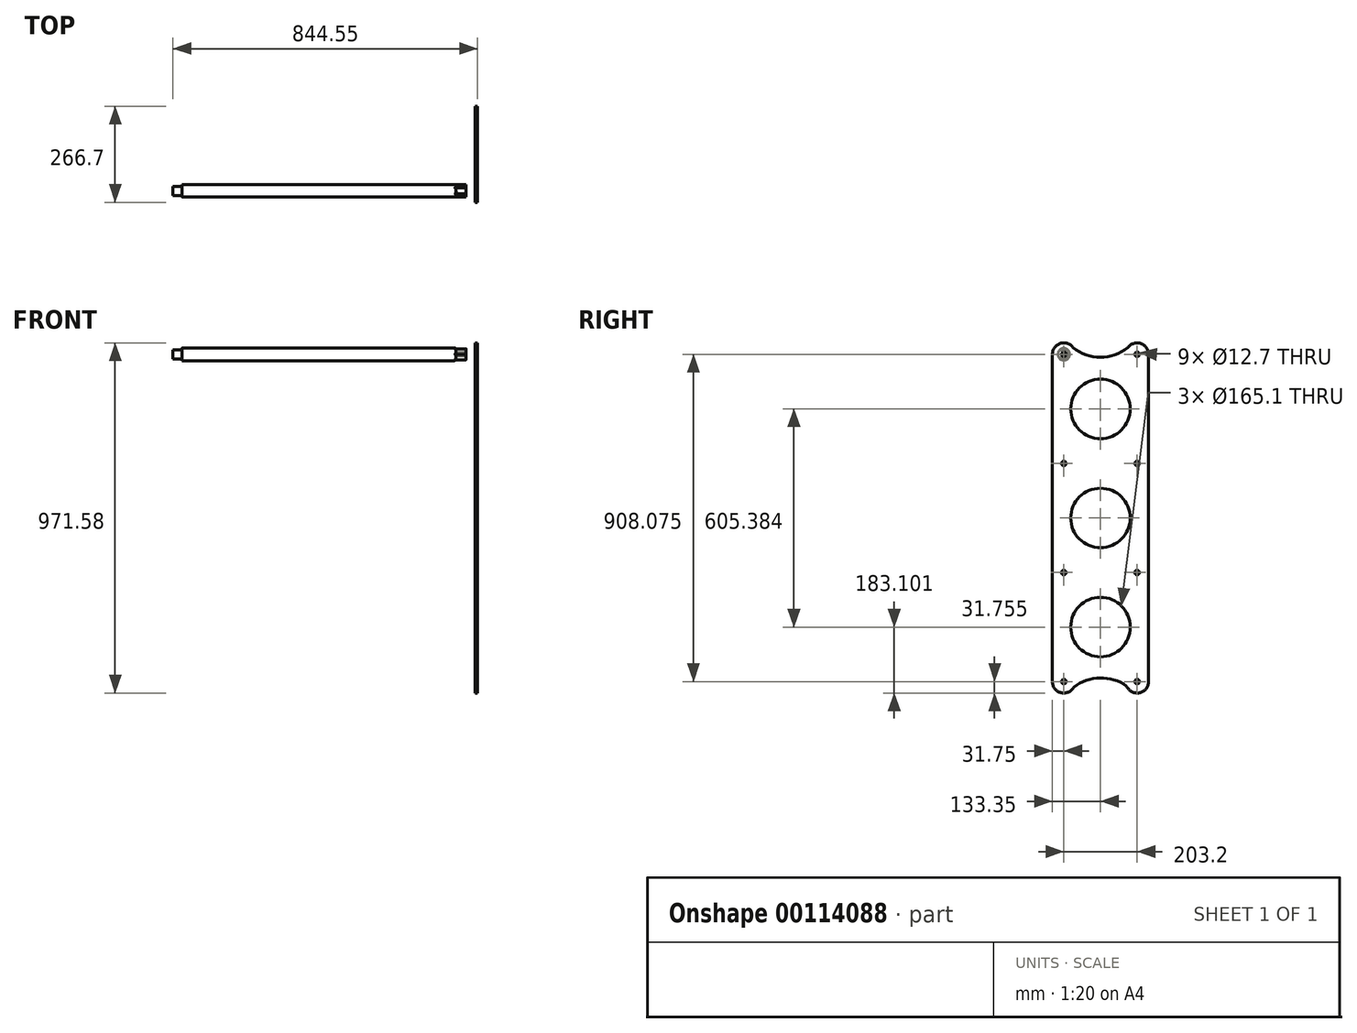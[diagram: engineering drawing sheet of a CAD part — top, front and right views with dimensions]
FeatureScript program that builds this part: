
annotation { "Feature Type Name" : "Feature", "Feature Type Description" : "" }
export const myFeature = defineFeature(function(context is Context, id is Id, definition is map)
    precondition{}
    {
        {
            var Q0;
            Q0=qCreatedBy(makeId("Right.planeOp"),FACE);
            var sketch = newSketch(context, id + "F0", { "sketchPlane" : qUnion([Q0])});
            skCircle(sketch, "E0", {"center": v(0, 0) * mm, "radius": 12.57 * mm});
            skSolve(sketch);
        }
        {
            var Q0;
            Q0 = qSketchRegion(id + "F0", true);
            extrude(context, id + "F1", {"entities" : qUnion([Q0]), "depth" : 25.4 * mm});
        }
        {
            var Q0;
            Q0=makeQuery(id+"F1.opExtrude","CAP_FACE",FACE,{"disambiguationData":[OSD([sQuery(id+"F0.wireOp",EDGE,"E0")])],"isStart":false});
            var sketch = newSketch(context, id + "F2", { "sketchPlane" : qUnion([Q0])});
            skCircle(sketch, "E1", {"center": v(0, 0) * mm, "radius": 17.53 * mm});
            skSolve(sketch);
        }
        {
            var Q0;
            Q0 = qSketchRegion(id + "F2", true);
            extrude(context, id + "F3", {"entities" : qUnion([Q0]), "operationType" : NewBodyOperationType.ADD, "depth" : 787.4 * mm});
        }
        {
            var Q0;
            Q0=makeQuery(id+"F3.opExtrude","CAP_FACE",FACE,{"disambiguationData":[OSD([sQuery(id+"F2.wireOp",EDGE,"E1")])],"isStart":false});
            var sketch = newSketch(context, id + "F4", { "sketchPlane" : qUnion([Q0])});
            skPoint(sketch, "E2", {"position": v(0, 0) * mm});
            skSolve(sketch);
        }
        {
            var Q0;
            Q0=sQuery(id+"F4.wireOp",VERTEX,"E2");
            var Q1;
            Q1=makeQuery(id+"F1.opExtrude","SWEPT_BODY",BODY,{"disambiguationData":[OSD([sQuery(id+"F0.wireOp",EDGE,"E0")])]});
            hole(context, id + "F5", {"style" : HoleStyle.SIMPLE, "endStyle" : HoleEndStyle.BLIND, "holeDiameter" : 12.7 * mm, "holeDepth" : 25.4 * mm, "startFromSketch" : true, "locations" : qUnion([Q0]), "scope" : qUnion([Q1])});
        }
        {
            var Q0;
            Q0=makeQuery(id+"F3.opExtrude","CAP_FACE",FACE,{"disambiguationData":[OSD([sQuery(id+"F2.wireOp",EDGE,"E1")])],"isStart":false});
            var sketch = newSketch(context, id + "F6", { "sketchPlane" : qUnion([Q0])});
            skCircle(sketch, "E3.cCircle", {"center": v(0, 0) * mm, "radius": 15.23 * mm, "construction": true});
            skLineSegment(sketch, "E3.0", {"start": v(-8.8, 15.23) * mm, "end": v(8.8, 15.23) * mm});
            skLineSegment(sketch, "E3.1", {"start": v(8.8, 15.23) * mm, "end": v(17.59, 0) * mm});
            skLineSegment(sketch, "E3.2", {"start": v(17.59, 0) * mm, "end": v(8.8, -15.23) * mm});
            skLineSegment(sketch, "E3.3", {"start": v(8.8, -15.23) * mm, "end": v(-8.8, -15.23) * mm});
            skLineSegment(sketch, "E3.4", {"start": v(-8.8, -15.23) * mm, "end": v(-17.59, 0) * mm});
            skLineSegment(sketch, "E3.5", {"start": v(-17.59, 0) * mm, "end": v(-8.8, 15.23) * mm});
            skPoint(sketch, "E3.0.midPoint", {"position": v(0, 15.23) * mm});
            skCircle(sketch, "E4", {"center": v(0, 0) * mm, "radius": 17.59 * mm});
            skSolve(sketch);
        }
        {
            var Q0;
            Q0=makeQuery(id+"F6.imprint","IMPRINT",FACE,{"disambiguationData":[TD([[makeQuery(id+"F6.imprint","IMPRINT",EDGE,{"derivedFrom":makeQuery(id+"F5.hole-0.boolean.opBoolean","COPY",EDGE,{"derivedFrom":makeQuery(id+"F5.hole-0.opRevolve","SWEPT_EDGE",EDGE,{"disambiguationData":[OSD([sQuery(id+"F5.hole-0.sketch.wireOp",EDGE,"core_line_2"),sQuery(id+"F5.hole-0.sketch.wireOp",EDGE,"core_line_3")])]})})}),1.0]])]});
            var Q1;
            {var subQ0=sQuery(id+"F6.wireOp",EDGE,"E3.0");var subQ1=makeQuery(id+"F3.opExtrude","CAP_EDGE",EDGE,{"disambiguationData":[OSD([sQuery(id+"F2.wireOp",EDGE,"E1")])],"isStart":false});var subQ2=makeQuery(id+"F6.imprint","INTERSECT",VERTEX,{"disambiguationData":[OD(0.0)],"derivedFrom":[subQ1,subQ0]});Q1=makeQuery(id+"F6.imprint","IMPRINT",FACE,{"disambiguationData":[TD([[makeQuery(id+"F6.imprint","IMPRINT",EDGE,{"disambiguationData":[TD([[subQ2,-1.0]])],"derivedFrom":subQ0}),1.0]])]});}
            var Q2;
            {var subQ0=sQuery(id+"F6.wireOp",EDGE,"E3.1");var subQ1=makeQuery(id+"F3.opExtrude","CAP_EDGE",EDGE,{"disambiguationData":[OSD([sQuery(id+"F2.wireOp",EDGE,"E1")])],"isStart":false});var subQ2=makeQuery(id+"F6.imprint","INTERSECT",VERTEX,{"disambiguationData":[OD(0.0)],"derivedFrom":[subQ1,subQ0]});Q2=makeQuery(id+"F6.imprint","IMPRINT",FACE,{"disambiguationData":[TD([[makeQuery(id+"F6.imprint","IMPRINT",EDGE,{"disambiguationData":[TD([[subQ2,-1.0]])],"derivedFrom":subQ0}),1.0]])]});}
            var Q3;
            {var subQ0=sQuery(id+"F6.wireOp",EDGE,"E3.2");var subQ1=makeQuery(id+"F3.opExtrude","CAP_EDGE",EDGE,{"disambiguationData":[OSD([sQuery(id+"F2.wireOp",EDGE,"E1")])],"isStart":false});var subQ2=makeQuery(id+"F6.imprint","INTERSECT",VERTEX,{"disambiguationData":[OD(0.0)],"derivedFrom":[subQ1,subQ0]});Q3=makeQuery(id+"F6.imprint","IMPRINT",FACE,{"disambiguationData":[TD([[makeQuery(id+"F6.imprint","IMPRINT",EDGE,{"disambiguationData":[TD([[subQ2,-1.0]])],"derivedFrom":subQ0}),1.0]])]});}
            var Q4;
            {var subQ0=sQuery(id+"F6.wireOp",EDGE,"E3.3");var subQ1=makeQuery(id+"F3.opExtrude","CAP_EDGE",EDGE,{"disambiguationData":[OSD([sQuery(id+"F2.wireOp",EDGE,"E1")])],"isStart":false});var subQ2=makeQuery(id+"F6.imprint","INTERSECT",VERTEX,{"disambiguationData":[OD(0.0)],"derivedFrom":[subQ1,subQ0]});Q4=makeQuery(id+"F6.imprint","IMPRINT",FACE,{"disambiguationData":[TD([[makeQuery(id+"F6.imprint","IMPRINT",EDGE,{"disambiguationData":[TD([[subQ2,-1.0]])],"derivedFrom":subQ0}),1.0]])]});}
            var Q5;
            {var subQ0=sQuery(id+"F6.wireOp",EDGE,"E3.4");var subQ1=makeQuery(id+"F3.opExtrude","CAP_EDGE",EDGE,{"disambiguationData":[OSD([sQuery(id+"F2.wireOp",EDGE,"E1")])],"isStart":false});var subQ2=makeQuery(id+"F6.imprint","INTERSECT",VERTEX,{"disambiguationData":[OD(0.0)],"derivedFrom":[subQ1,subQ0]});Q5=makeQuery(id+"F6.imprint","IMPRINT",FACE,{"disambiguationData":[TD([[makeQuery(id+"F6.imprint","IMPRINT",EDGE,{"disambiguationData":[TD([[subQ2,-1.0]])],"derivedFrom":subQ0}),1.0]])]});}
            var Q6;
            {var subQ0=sQuery(id+"F6.wireOp",EDGE,"E3.5");var subQ1=makeQuery(id+"F3.opExtrude","CAP_EDGE",EDGE,{"disambiguationData":[OSD([sQuery(id+"F2.wireOp",EDGE,"E1")])],"isStart":false});var subQ2=makeQuery(id+"F6.imprint","INTERSECT",VERTEX,{"disambiguationData":[OD(0.0)],"derivedFrom":[subQ1,subQ0]});Q6=makeQuery(id+"F6.imprint","IMPRINT",FACE,{"disambiguationData":[TD([[makeQuery(id+"F6.imprint","IMPRINT",EDGE,{"disambiguationData":[TD([[subQ2,-1.0]])],"derivedFrom":subQ0}),1.0]])]});}
            var Q7;
            {var subQ1=sQuery(id+"F6.wireOp",EDGE,"E3.0");var subQ3=makeQuery(id+"F3.opExtrude","CAP_EDGE",EDGE,{"disambiguationData":[OSD([sQuery(id+"F2.wireOp",EDGE,"E1")])],"isStart":false});var subQ4=makeQuery(id+"F6.imprint","INTERSECT",VERTEX,{"disambiguationData":[OD(0.0)],"derivedFrom":[subQ3,subQ1]});Q7=makeQuery(id+"F6.imprint","IMPRINT",FACE,{"disambiguationData":[TD([[makeQuery(id+"F6.imprint","IMPRINT",EDGE,{"disambiguationData":[TD([[subQ4,1.0]])],"derivedFrom":subQ3}),-1.0]])]});}
            var Q8;
            {var subQ1=sQuery(id+"F6.wireOp",EDGE,"E3.0");var subQ3=makeQuery(id+"F3.opExtrude","CAP_EDGE",EDGE,{"disambiguationData":[OSD([sQuery(id+"F2.wireOp",EDGE,"E1")])],"isStart":false});var subQ4=makeQuery(id+"F6.imprint","INTERSECT",VERTEX,{"disambiguationData":[OD(0.0)],"derivedFrom":[subQ3,subQ1]});Q8=makeQuery(id+"F6.imprint","IMPRINT",FACE,{"disambiguationData":[TD([[makeQuery(id+"F6.imprint","IMPRINT",EDGE,{"disambiguationData":[TD([[subQ4,-1.0]])],"derivedFrom":subQ3}),-1.0]])]});}
            var Q9;
            {var subQ1=sQuery(id+"F6.wireOp",EDGE,"E3.0");var subQ3=makeQuery(id+"F3.opExtrude","CAP_EDGE",EDGE,{"disambiguationData":[OSD([sQuery(id+"F2.wireOp",EDGE,"E1")])],"isStart":false});var subQ4=makeQuery(id+"F6.imprint","INTERSECT",VERTEX,{"disambiguationData":[OD(1.0)],"derivedFrom":[subQ3,subQ1]});Q9=makeQuery(id+"F6.imprint","IMPRINT",FACE,{"disambiguationData":[TD([[makeQuery(id+"F6.imprint","IMPRINT",EDGE,{"disambiguationData":[TD([[subQ4,1.0]])],"derivedFrom":subQ3}),-1.0]])]});}
            var Q10;
            {var subQ1=sQuery(id+"F6.wireOp",EDGE,"E3.1");var subQ3=makeQuery(id+"F3.opExtrude","CAP_EDGE",EDGE,{"disambiguationData":[OSD([sQuery(id+"F2.wireOp",EDGE,"E1")])],"isStart":false});var subQ4=makeQuery(id+"F6.imprint","INTERSECT",VERTEX,{"disambiguationData":[OD(0.0)],"derivedFrom":[subQ3,subQ1]});Q10=makeQuery(id+"F6.imprint","IMPRINT",FACE,{"disambiguationData":[TD([[makeQuery(id+"F6.imprint","IMPRINT",EDGE,{"disambiguationData":[TD([[subQ4,1.0]])],"derivedFrom":subQ3}),-1.0]])]});}
            var Q11;
            {var subQ1=sQuery(id+"F6.wireOp",EDGE,"E3.1");var subQ3=makeQuery(id+"F3.opExtrude","CAP_EDGE",EDGE,{"disambiguationData":[OSD([sQuery(id+"F2.wireOp",EDGE,"E1")])],"isStart":false});var subQ4=makeQuery(id+"F6.imprint","INTERSECT",VERTEX,{"disambiguationData":[OD(1.0)],"derivedFrom":[subQ3,subQ1]});Q11=makeQuery(id+"F6.imprint","IMPRINT",FACE,{"disambiguationData":[TD([[makeQuery(id+"F6.imprint","IMPRINT",EDGE,{"disambiguationData":[TD([[subQ4,1.0]])],"derivedFrom":subQ3}),-1.0]])]});}
            var Q12;
            {var subQ1=sQuery(id+"F6.wireOp",EDGE,"E3.2");var subQ3=makeQuery(id+"F3.opExtrude","CAP_EDGE",EDGE,{"disambiguationData":[OSD([sQuery(id+"F2.wireOp",EDGE,"E1")])],"isStart":false});var subQ4=makeQuery(id+"F6.imprint","INTERSECT",VERTEX,{"disambiguationData":[OD(0.0)],"derivedFrom":[subQ3,subQ1]});Q12=makeQuery(id+"F6.imprint","IMPRINT",FACE,{"disambiguationData":[TD([[makeQuery(id+"F6.imprint","IMPRINT",EDGE,{"disambiguationData":[TD([[subQ4,1.0]])],"derivedFrom":subQ3}),-1.0]])]});}
            var Q13;
            {var subQ1=sQuery(id+"F6.wireOp",EDGE,"E3.2");var subQ3=makeQuery(id+"F3.opExtrude","CAP_EDGE",EDGE,{"disambiguationData":[OSD([sQuery(id+"F2.wireOp",EDGE,"E1")])],"isStart":false});var subQ4=makeQuery(id+"F6.imprint","INTERSECT",VERTEX,{"disambiguationData":[OD(1.0)],"derivedFrom":[subQ3,subQ1]});Q13=makeQuery(id+"F6.imprint","IMPRINT",FACE,{"disambiguationData":[TD([[makeQuery(id+"F6.imprint","IMPRINT",EDGE,{"disambiguationData":[TD([[subQ4,1.0]])],"derivedFrom":subQ3}),-1.0]])]});}
            var Q14;
            {var subQ1=sQuery(id+"F6.wireOp",EDGE,"E3.3");var subQ3=makeQuery(id+"F3.opExtrude","CAP_EDGE",EDGE,{"disambiguationData":[OSD([sQuery(id+"F2.wireOp",EDGE,"E1")])],"isStart":false});var subQ4=makeQuery(id+"F6.imprint","INTERSECT",VERTEX,{"disambiguationData":[OD(0.0)],"derivedFrom":[subQ3,subQ1]});Q14=makeQuery(id+"F6.imprint","IMPRINT",FACE,{"disambiguationData":[TD([[makeQuery(id+"F6.imprint","IMPRINT",EDGE,{"disambiguationData":[TD([[subQ4,1.0]])],"derivedFrom":subQ3}),-1.0]])]});}
            var Q15;
            {var subQ1=sQuery(id+"F6.wireOp",EDGE,"E3.3");var subQ3=makeQuery(id+"F3.opExtrude","CAP_EDGE",EDGE,{"disambiguationData":[OSD([sQuery(id+"F2.wireOp",EDGE,"E1")])],"isStart":false});var subQ4=makeQuery(id+"F6.imprint","INTERSECT",VERTEX,{"disambiguationData":[OD(1.0)],"derivedFrom":[subQ3,subQ1]});Q15=makeQuery(id+"F6.imprint","IMPRINT",FACE,{"disambiguationData":[TD([[makeQuery(id+"F6.imprint","IMPRINT",EDGE,{"disambiguationData":[TD([[subQ4,1.0]])],"derivedFrom":subQ3}),-1.0]])]});}
            var Q16;
            {var subQ1=sQuery(id+"F6.wireOp",EDGE,"E3.4");var subQ3=makeQuery(id+"F3.opExtrude","CAP_EDGE",EDGE,{"disambiguationData":[OSD([sQuery(id+"F2.wireOp",EDGE,"E1")])],"isStart":false});var subQ4=makeQuery(id+"F6.imprint","INTERSECT",VERTEX,{"disambiguationData":[OD(0.0)],"derivedFrom":[subQ3,subQ1]});Q16=makeQuery(id+"F6.imprint","IMPRINT",FACE,{"disambiguationData":[TD([[makeQuery(id+"F6.imprint","IMPRINT",EDGE,{"disambiguationData":[TD([[subQ4,1.0]])],"derivedFrom":subQ3}),-1.0]])]});}
            var Q17;
            {var subQ1=sQuery(id+"F6.wireOp",EDGE,"E3.4");var subQ3=makeQuery(id+"F3.opExtrude","CAP_EDGE",EDGE,{"disambiguationData":[OSD([sQuery(id+"F2.wireOp",EDGE,"E1")])],"isStart":false});var subQ4=makeQuery(id+"F6.imprint","INTERSECT",VERTEX,{"disambiguationData":[OD(1.0)],"derivedFrom":[subQ3,subQ1]});Q17=makeQuery(id+"F6.imprint","IMPRINT",FACE,{"disambiguationData":[TD([[makeQuery(id+"F6.imprint","IMPRINT",EDGE,{"disambiguationData":[TD([[subQ4,1.0]])],"derivedFrom":subQ3}),-1.0]])]});}
            var Q18;
            {var subQ1=sQuery(id+"F6.wireOp",EDGE,"E3.5");var subQ3=makeQuery(id+"F3.opExtrude","CAP_EDGE",EDGE,{"disambiguationData":[OSD([sQuery(id+"F2.wireOp",EDGE,"E1")])],"isStart":false});var subQ4=makeQuery(id+"F6.imprint","INTERSECT",VERTEX,{"disambiguationData":[OD(0.0)],"derivedFrom":[subQ3,subQ1]});Q18=makeQuery(id+"F6.imprint","IMPRINT",FACE,{"disambiguationData":[TD([[makeQuery(id+"F6.imprint","IMPRINT",EDGE,{"disambiguationData":[TD([[subQ4,1.0]])],"derivedFrom":subQ3}),-1.0]])]});}
            extrude(context, id + "F7", {"entities" : qUnion([Q0, Q1, Q2, Q3, Q4, Q5, Q6, Q7, Q8, Q9, Q10, Q11, Q12, Q13, Q14, Q15, Q16, Q17, Q18]), "operationType" : NewBodyOperationType.REMOVE, "oppositeDirection" : true, "depth" : 25.4 * mm});
        }
        {
            var Q0;
            {var subQ0=sQuery(id+"F2.wireOp",EDGE,"E1");Q0=makeQuery(id+"F7.boolean.opBoolean","INTERSECT",EDGE,{"disambiguationData":[OD(1.0)],"derivedFrom":[makeQuery(id+"F3.opExtrude","SWEPT_FACE",FACE,{"disambiguationData":[OSD([subQ0])]}),makeQuery(id+"F7.opExtrude","CAP_FACE",FACE,{"disambiguationData":[OSD([subQ0,sQuery(id+"F6.wireOp",EDGE,"E3.0"),sQuery(id+"F6.wireOp",EDGE,"E3.1"),sQuery(id+"F6.wireOp",EDGE,"E3.2"),sQuery(id+"F6.wireOp",EDGE,"E3.3"),sQuery(id+"F6.wireOp",EDGE,"E3.4"),sQuery(id+"F6.wireOp",EDGE,"E3.5"),sQuery(id+"F6.wireOp",EDGE,"E4")])],"isStart":false})]});}
            var Q1;
            {var subQ0=sQuery(id+"F2.wireOp",EDGE,"E1");Q1=makeQuery(id+"F7.boolean.opBoolean","INTERSECT",EDGE,{"disambiguationData":[OD(0.0)],"derivedFrom":[makeQuery(id+"F3.opExtrude","SWEPT_FACE",FACE,{"disambiguationData":[OSD([subQ0])]}),makeQuery(id+"F7.opExtrude","CAP_FACE",FACE,{"disambiguationData":[OSD([subQ0,sQuery(id+"F6.wireOp",EDGE,"E3.0"),sQuery(id+"F6.wireOp",EDGE,"E3.1"),sQuery(id+"F6.wireOp",EDGE,"E3.2"),sQuery(id+"F6.wireOp",EDGE,"E3.3"),sQuery(id+"F6.wireOp",EDGE,"E3.4"),sQuery(id+"F6.wireOp",EDGE,"E3.5"),sQuery(id+"F6.wireOp",EDGE,"E4")])],"isStart":false})]});}
            var Q2;
            {var subQ0=sQuery(id+"F2.wireOp",EDGE,"E1");Q2=makeQuery(id+"F7.boolean.opBoolean","INTERSECT",EDGE,{"disambiguationData":[OD(2.0)],"derivedFrom":[makeQuery(id+"F3.opExtrude","SWEPT_FACE",FACE,{"disambiguationData":[OSD([subQ0])]}),makeQuery(id+"F7.opExtrude","CAP_FACE",FACE,{"disambiguationData":[OSD([subQ0,sQuery(id+"F6.wireOp",EDGE,"E3.0"),sQuery(id+"F6.wireOp",EDGE,"E3.1"),sQuery(id+"F6.wireOp",EDGE,"E3.2"),sQuery(id+"F6.wireOp",EDGE,"E3.3"),sQuery(id+"F6.wireOp",EDGE,"E3.4"),sQuery(id+"F6.wireOp",EDGE,"E3.5"),sQuery(id+"F6.wireOp",EDGE,"E4")])],"isStart":false})]});}
            var Q3;
            {var subQ0=sQuery(id+"F2.wireOp",EDGE,"E1");Q3=makeQuery(id+"F7.boolean.opBoolean","INTERSECT",EDGE,{"disambiguationData":[OD(3.0)],"derivedFrom":[makeQuery(id+"F3.opExtrude","SWEPT_FACE",FACE,{"disambiguationData":[OSD([subQ0])]}),makeQuery(id+"F7.opExtrude","CAP_FACE",FACE,{"disambiguationData":[OSD([subQ0,sQuery(id+"F6.wireOp",EDGE,"E3.0"),sQuery(id+"F6.wireOp",EDGE,"E3.1"),sQuery(id+"F6.wireOp",EDGE,"E3.2"),sQuery(id+"F6.wireOp",EDGE,"E3.3"),sQuery(id+"F6.wireOp",EDGE,"E3.4"),sQuery(id+"F6.wireOp",EDGE,"E3.5"),sQuery(id+"F6.wireOp",EDGE,"E4")])],"isStart":false})]});}
            var Q4;
            {var subQ0=sQuery(id+"F2.wireOp",EDGE,"E1");Q4=makeQuery(id+"F7.boolean.opBoolean","INTERSECT",EDGE,{"disambiguationData":[OD(4.0)],"derivedFrom":[makeQuery(id+"F3.opExtrude","SWEPT_FACE",FACE,{"disambiguationData":[OSD([subQ0])]}),makeQuery(id+"F7.opExtrude","CAP_FACE",FACE,{"disambiguationData":[OSD([subQ0,sQuery(id+"F6.wireOp",EDGE,"E3.0"),sQuery(id+"F6.wireOp",EDGE,"E3.1"),sQuery(id+"F6.wireOp",EDGE,"E3.2"),sQuery(id+"F6.wireOp",EDGE,"E3.3"),sQuery(id+"F6.wireOp",EDGE,"E3.4"),sQuery(id+"F6.wireOp",EDGE,"E3.5"),sQuery(id+"F6.wireOp",EDGE,"E4")])],"isStart":false})]});}
            var Q5;
            {var subQ0=sQuery(id+"F2.wireOp",EDGE,"E1");Q5=makeQuery(id+"F7.boolean.opBoolean","INTERSECT",EDGE,{"disambiguationData":[OD(5.0)],"derivedFrom":[makeQuery(id+"F3.opExtrude","SWEPT_FACE",FACE,{"disambiguationData":[OSD([subQ0])]}),makeQuery(id+"F7.opExtrude","CAP_FACE",FACE,{"disambiguationData":[OSD([subQ0,sQuery(id+"F6.wireOp",EDGE,"E3.0"),sQuery(id+"F6.wireOp",EDGE,"E3.1"),sQuery(id+"F6.wireOp",EDGE,"E3.2"),sQuery(id+"F6.wireOp",EDGE,"E3.3"),sQuery(id+"F6.wireOp",EDGE,"E3.4"),sQuery(id+"F6.wireOp",EDGE,"E3.5"),sQuery(id+"F6.wireOp",EDGE,"E4")])],"isStart":false})]});}
            chamfer(context, id + "F8", {"entities" : qUnion([Q0, Q1, Q2, Q3, Q4, Q5]), "width" : 5.08 * mm, "tangentPropagation" : true});
        }
        {
            var Q0;
            {var subQ0=sQuery(id+"F2.wireOp",EDGE,"E1");var subQ1=makeQuery(id+"F3.opExtrude","SWEPT_FACE",FACE,{"disambiguationData":[OSD([subQ0])]});Q0=makeQuery(id+"F8.opChamfer","BLEND_EDGE",EDGE,{"blendedFrom":[makeQuery(id+"F7.boolean.opBoolean","INTERSECT",EDGE,{"disambiguationData":[OD(5.0)],"derivedFrom":[subQ1,makeQuery(id+"F7.opExtrude","CAP_FACE",FACE,{"disambiguationData":[OSD([subQ0,sQuery(id+"F6.wireOp",EDGE,"E3.0"),sQuery(id+"F6.wireOp",EDGE,"E3.1"),sQuery(id+"F6.wireOp",EDGE,"E3.2"),sQuery(id+"F6.wireOp",EDGE,"E3.3"),sQuery(id+"F6.wireOp",EDGE,"E3.4"),sQuery(id+"F6.wireOp",EDGE,"E3.5"),sQuery(id+"F6.wireOp",EDGE,"E4")])],"isStart":false})]}),subQ1],"blendedInto":[subQ1]});}
            var Q1;
            {var subQ0=sQuery(id+"F2.wireOp",EDGE,"E1");var subQ1=makeQuery(id+"F3.opExtrude","SWEPT_FACE",FACE,{"disambiguationData":[OSD([subQ0])]});Q1=makeQuery(id+"F8.opChamfer","BLEND_EDGE",EDGE,{"blendedFrom":[makeQuery(id+"F7.boolean.opBoolean","INTERSECT",EDGE,{"disambiguationData":[OD(4.0)],"derivedFrom":[subQ1,makeQuery(id+"F7.opExtrude","CAP_FACE",FACE,{"disambiguationData":[OSD([subQ0,sQuery(id+"F6.wireOp",EDGE,"E3.0"),sQuery(id+"F6.wireOp",EDGE,"E3.1"),sQuery(id+"F6.wireOp",EDGE,"E3.2"),sQuery(id+"F6.wireOp",EDGE,"E3.3"),sQuery(id+"F6.wireOp",EDGE,"E3.4"),sQuery(id+"F6.wireOp",EDGE,"E3.5"),sQuery(id+"F6.wireOp",EDGE,"E4")])],"isStart":false})]}),subQ1],"blendedInto":[subQ1]});}
            var Q2;
            {var subQ0=sQuery(id+"F2.wireOp",EDGE,"E1");var subQ1=makeQuery(id+"F3.opExtrude","SWEPT_FACE",FACE,{"disambiguationData":[OSD([subQ0])]});Q2=makeQuery(id+"F8.opChamfer","BLEND_EDGE",EDGE,{"blendedFrom":[makeQuery(id+"F7.boolean.opBoolean","INTERSECT",EDGE,{"disambiguationData":[OD(0.0)],"derivedFrom":[subQ1,makeQuery(id+"F7.opExtrude","CAP_FACE",FACE,{"disambiguationData":[OSD([subQ0,sQuery(id+"F6.wireOp",EDGE,"E3.0"),sQuery(id+"F6.wireOp",EDGE,"E3.1"),sQuery(id+"F6.wireOp",EDGE,"E3.2"),sQuery(id+"F6.wireOp",EDGE,"E3.3"),sQuery(id+"F6.wireOp",EDGE,"E3.4"),sQuery(id+"F6.wireOp",EDGE,"E3.5"),sQuery(id+"F6.wireOp",EDGE,"E4")])],"isStart":false})]}),subQ1],"blendedInto":[subQ1]});}
            var Q3;
            {var subQ0=sQuery(id+"F2.wireOp",EDGE,"E1");var subQ1=makeQuery(id+"F3.opExtrude","SWEPT_FACE",FACE,{"disambiguationData":[OSD([subQ0])]});Q3=makeQuery(id+"F8.opChamfer","BLEND_EDGE",EDGE,{"blendedFrom":[makeQuery(id+"F7.boolean.opBoolean","INTERSECT",EDGE,{"disambiguationData":[OD(3.0)],"derivedFrom":[subQ1,makeQuery(id+"F7.opExtrude","CAP_FACE",FACE,{"disambiguationData":[OSD([subQ0,sQuery(id+"F6.wireOp",EDGE,"E3.0"),sQuery(id+"F6.wireOp",EDGE,"E3.1"),sQuery(id+"F6.wireOp",EDGE,"E3.2"),sQuery(id+"F6.wireOp",EDGE,"E3.3"),sQuery(id+"F6.wireOp",EDGE,"E3.4"),sQuery(id+"F6.wireOp",EDGE,"E3.5"),sQuery(id+"F6.wireOp",EDGE,"E4")])],"isStart":false})]}),subQ1],"blendedInto":[subQ1]});}
            var Q4;
            {var subQ0=sQuery(id+"F2.wireOp",EDGE,"E1");var subQ1=makeQuery(id+"F3.opExtrude","SWEPT_FACE",FACE,{"disambiguationData":[OSD([subQ0])]});Q4=makeQuery(id+"F8.opChamfer","BLEND_EDGE",EDGE,{"blendedFrom":[makeQuery(id+"F7.boolean.opBoolean","INTERSECT",EDGE,{"disambiguationData":[OD(2.0)],"derivedFrom":[subQ1,makeQuery(id+"F7.opExtrude","CAP_FACE",FACE,{"disambiguationData":[OSD([subQ0,sQuery(id+"F6.wireOp",EDGE,"E3.0"),sQuery(id+"F6.wireOp",EDGE,"E3.1"),sQuery(id+"F6.wireOp",EDGE,"E3.2"),sQuery(id+"F6.wireOp",EDGE,"E3.3"),sQuery(id+"F6.wireOp",EDGE,"E3.4"),sQuery(id+"F6.wireOp",EDGE,"E3.5"),sQuery(id+"F6.wireOp",EDGE,"E4")])],"isStart":false})]}),subQ1],"blendedInto":[subQ1]});}
            var Q5;
            {var subQ0=sQuery(id+"F2.wireOp",EDGE,"E1");var subQ1=makeQuery(id+"F3.opExtrude","SWEPT_FACE",FACE,{"disambiguationData":[OSD([subQ0])]});Q5=makeQuery(id+"F8.opChamfer","BLEND_EDGE",EDGE,{"blendedFrom":[makeQuery(id+"F7.boolean.opBoolean","INTERSECT",EDGE,{"disambiguationData":[OD(1.0)],"derivedFrom":[subQ1,makeQuery(id+"F7.opExtrude","CAP_FACE",FACE,{"disambiguationData":[OSD([subQ0,sQuery(id+"F6.wireOp",EDGE,"E3.0"),sQuery(id+"F6.wireOp",EDGE,"E3.1"),sQuery(id+"F6.wireOp",EDGE,"E3.2"),sQuery(id+"F6.wireOp",EDGE,"E3.3"),sQuery(id+"F6.wireOp",EDGE,"E3.4"),sQuery(id+"F6.wireOp",EDGE,"E3.5"),sQuery(id+"F6.wireOp",EDGE,"E4")])],"isStart":false})]}),subQ1],"blendedInto":[subQ1]});}
            fillet(context, id + "F9", {"entities" : qUnion([Q0, Q1, Q2, Q3, Q4, Q5]), "radius" : 5.08 * mm, "tangentPropagation" : true, "allowEdgeOverflow" : false});
        }
        {
            var Q0;
            Q0=makeQuery(id+"F3.opExtrude","CAP_FACE",FACE,{"disambiguationData":[OSD([sQuery(id+"F2.wireOp",EDGE,"E1")])],"isStart":false});
            cPlane(context, id + "F10", {"entities" : qUnion([Q0]), "cplaneType" : CPlaneType.OFFSET, "offset" : 25.4 * mm, "width" : 152.4 * mm, "height" : 152.4 * mm});
        }
        {
            var Q0;
            Q0=qCreatedBy(id+"F10.planeOp",FACE);
            var sketch = newSketch(context, id + "F11", { "sketchPlane" : qUnion([Q0])});
            skCircle(sketch, "E5", {"center": v(0, 0) * mm, "radius": 6.35 * mm});
            skLineSegment(sketch, "E6", {"start": v(0, 0) * mm, "end": v(6.35, 0) * mm, "construction": true});
            skCircle(sketch, "E7", {"center": v(203.2, 0) * mm, "radius": 6.35 * mm});
            skLineSegment(sketch, "E8", {"start": v(0, 0) * mm, "end": v(0, -6.35) * mm, "construction": true});
            skLineSegment(sketch, "E9", {"start": v(0, -302.7) * mm, "end": v(0, -309.04) * mm, "construction": true});
            skLineSegment(sketch, "E10", {"start": v(0, -605.38) * mm, "end": v(0, -611.73) * mm, "construction": true});
            skCircle(sketch, "E11", {"center": v(0, -302.7) * mm, "radius": 6.35 * mm});
            skCircle(sketch, "E12", {"center": v(0, -605.38) * mm, "radius": 6.35 * mm});
            skCircle(sketch, "E13", {"center": v(0, -908.08) * mm, "radius": 6.35 * mm});
            skCircle(sketch, "E14", {"center": v(203.2, -302.7) * mm, "radius": 6.35 * mm});
            skCircle(sketch, "E15", {"center": v(203.2, -605.38) * mm, "radius": 6.35 * mm});
            skCircle(sketch, "E16", {"center": v(203.2, -908.08) * mm, "radius": 6.35 * mm});
            skArc(sketch, "E17", {"start": v(25.4, 19.04) * mm, "mid": v(-10.04, 30.12) * mm, "end": v(-31.75, 0) * mm});
            skArc(sketch, "E18", {"start": v(234.95, 0) * mm, "mid": v(213.08, 30.17) * mm, "end": v(177.6, 18.78) * mm});
            skArc(sketch, "E19", {"start": v(174.02, -920.6) * mm, "mid": v(209.6, -939.18) * mm, "end": v(234.95, -908.08) * mm});
            skArc(sketch, "E20", {"start": v(-31.75, -908.08) * mm, "mid": v(-7.98, -938.8) * mm, "end": v(27.74, -923.52) * mm});
            skLineSegment(sketch, "E21", {"start": v(-31.75, 0) * mm, "end": v(-31.75, -908.08) * mm});
            skLineSegment(sketch, "E22", {"start": v(234.95, -908.08) * mm, "end": v(234.95, 0) * mm});
            skArc(sketch, "E23", {"start": v(25.4, 19.04) * mm, "mid": v(101.46, -7.8) * mm, "end": v(177.6, 18.78) * mm});
            skArc(sketch, "E24", {"start": v(174.02, -920.6) * mm, "mid": v(100.4, -897.78) * mm, "end": v(27.74, -923.52) * mm});
            skLineSegment(sketch, "E25.trimOffspring", {"start": v(0, -901.73) * mm, "end": v(0, -908.08) * mm, "construction": true});
            skLineSegment(sketch, "E26.trimOffspring", {"start": v(196.85, 0) * mm, "end": v(203.2, 0) * mm, "construction": true});
            skLineSegment(sketch, "E27.trimOffspring", {"start": v(0, -599.03) * mm, "end": v(0, -605.38) * mm, "construction": true});
            skLineSegment(sketch, "E28.trimOffspring", {"start": v(0, -296.34) * mm, "end": v(0, -302.7) * mm, "construction": true});
            skLineSegment(sketch, "E29", {"start": v(0, 0) * mm, "end": v(203.2, -302.7) * mm, "construction": true});
            skLineSegment(sketch, "E30", {"start": v(203.2, 0) * mm, "end": v(0, -302.7) * mm, "construction": true});
            skLineSegment(sketch, "E31", {"start": v(203.2, -302.7) * mm, "end": v(0, -605.38) * mm, "construction": true});
            skLineSegment(sketch, "E32", {"start": v(0, -302.7) * mm, "end": v(203.2, -605.38) * mm, "construction": true});
            skLineSegment(sketch, "E33", {"start": v(0, -908.08) * mm, "end": v(203.2, -605.38) * mm, "construction": true});
            skLineSegment(sketch, "E34", {"start": v(0, -605.38) * mm, "end": v(203.2, -908.08) * mm, "construction": true});
            skCircle(sketch, "E35", {"center": v(101.6, -756.73) * mm, "radius": 82.55 * mm});
            skCircle(sketch, "E36", {"center": v(101.6, -454.04) * mm, "radius": 82.55 * mm});
            skCircle(sketch, "E37", {"center": v(101.6, -151.35) * mm, "radius": 82.55 * mm});
            skSolve(sketch);
        }
        {
            var Q0;
            Q0 = qSketchRegion(id + "F11", true);
            extrude(context, id + "F12", {"entities" : qUnion([Q0]), "depth" : 6.35 * mm});
        }
        {
            var Q0;
            Q0=makeQuery(id+"F12.opExtrude","CAP_FACE",FACE,{"disambiguationData":[OSD([sQuery(id+"F11.wireOp",EDGE,"E5"),sQuery(id+"F11.wireOp",EDGE,"E7"),sQuery(id+"F11.wireOp",EDGE,"E11"),sQuery(id+"F11.wireOp",EDGE,"E12"),sQuery(id+"F11.wireOp",EDGE,"E13"),sQuery(id+"F11.wireOp",EDGE,"E14"),sQuery(id+"F11.wireOp",EDGE,"E15"),sQuery(id+"F11.wireOp",EDGE,"E16"),sQuery(id+"F11.wireOp",EDGE,"E17"),sQuery(id+"F11.wireOp",EDGE,"E18"),sQuery(id+"F11.wireOp",EDGE,"E19"),sQuery(id+"F11.wireOp",EDGE,"E20"),sQuery(id+"F11.wireOp",EDGE,"E21"),sQuery(id+"F11.wireOp",EDGE,"E22"),sQuery(id+"F11.wireOp",EDGE,"E23"),sQuery(id+"F11.wireOp",EDGE,"E24"),sQuery(id+"F11.wireOp",EDGE,"E35"),sQuery(id+"F11.wireOp",EDGE,"E36"),sQuery(id+"F11.wireOp",EDGE,"E37")])],"isStart":false});
            var sketch = newSketch(context, id + "F13", { "sketchPlane" : qUnion([Q0])});
            skSolve(sketch);
        }
        {
            var Q0;
            Q0=makeQuery(id+"F13.imprint","IMPRINT",FACE,{"disambiguationData":[TD([[makeQuery(id+"F13.imprint","IMPRINT",EDGE,{"derivedFrom":makeQuery(id+"F12.opExtrude","CAP_EDGE",EDGE,{"disambiguationData":[OSD([sQuery(id+"F11.wireOp",EDGE,"E37")])],"isStart":false})}),1.0]])]});
            extrude(context, id + "F14", {"entities" : qUnion([Q0]), "operationType" : NewBodyOperationType.REMOVE, "oppositeDirection" : true, "depth" : 25.4 * mm});
        }
    });
